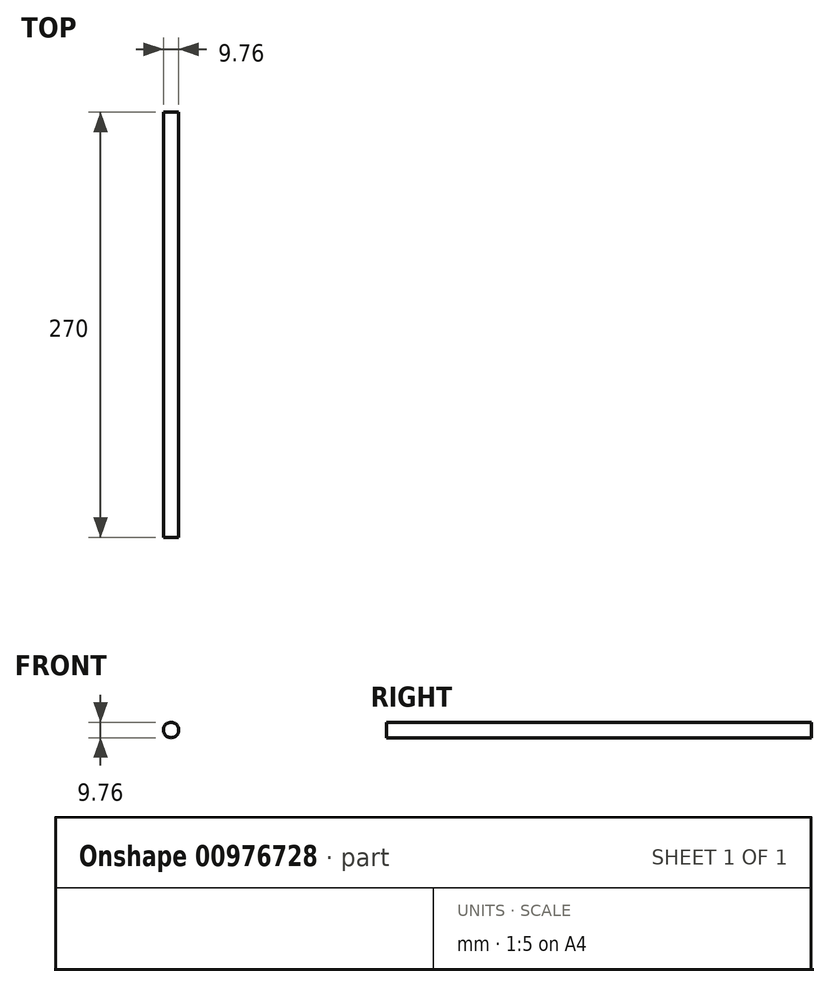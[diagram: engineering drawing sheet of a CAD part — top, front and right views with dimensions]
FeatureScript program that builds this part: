
annotation { "Feature Type Name" : "Feature", "Feature Type Description" : "" }
export const myFeature = defineFeature(function(context is Context, id is Id, definition is map)
    precondition{}
    {
        {
            var Q0;
            Q0=qCreatedBy(makeId("Front.planeOp"),FACE);
            var sketch = newSketch(context, id + "F0", { "sketchPlane" : qUnion([Q0])});
            skCircle(sketch, "E0", {"center": v(0, 0) * mm, "radius": 4.88 * mm});
            skSolve(sketch);
        }
        {
            var Q0;
            Q0=makeQuery(id+"F0.imprint","IMPRINT",FACE,{"disambiguationData":[TD([[makeQuery(id+"F0.imprint","IMPRINT",EDGE,{"derivedFrom":sQuery(id+"F0.wireOp",EDGE,"E0")}),1.0]])]});
            extrude(context, id + "F1", {"entities" : qUnion([Q0]), "depth" : 270 * mm, "offsetDistance" : 25 * mm});
        }
    });
